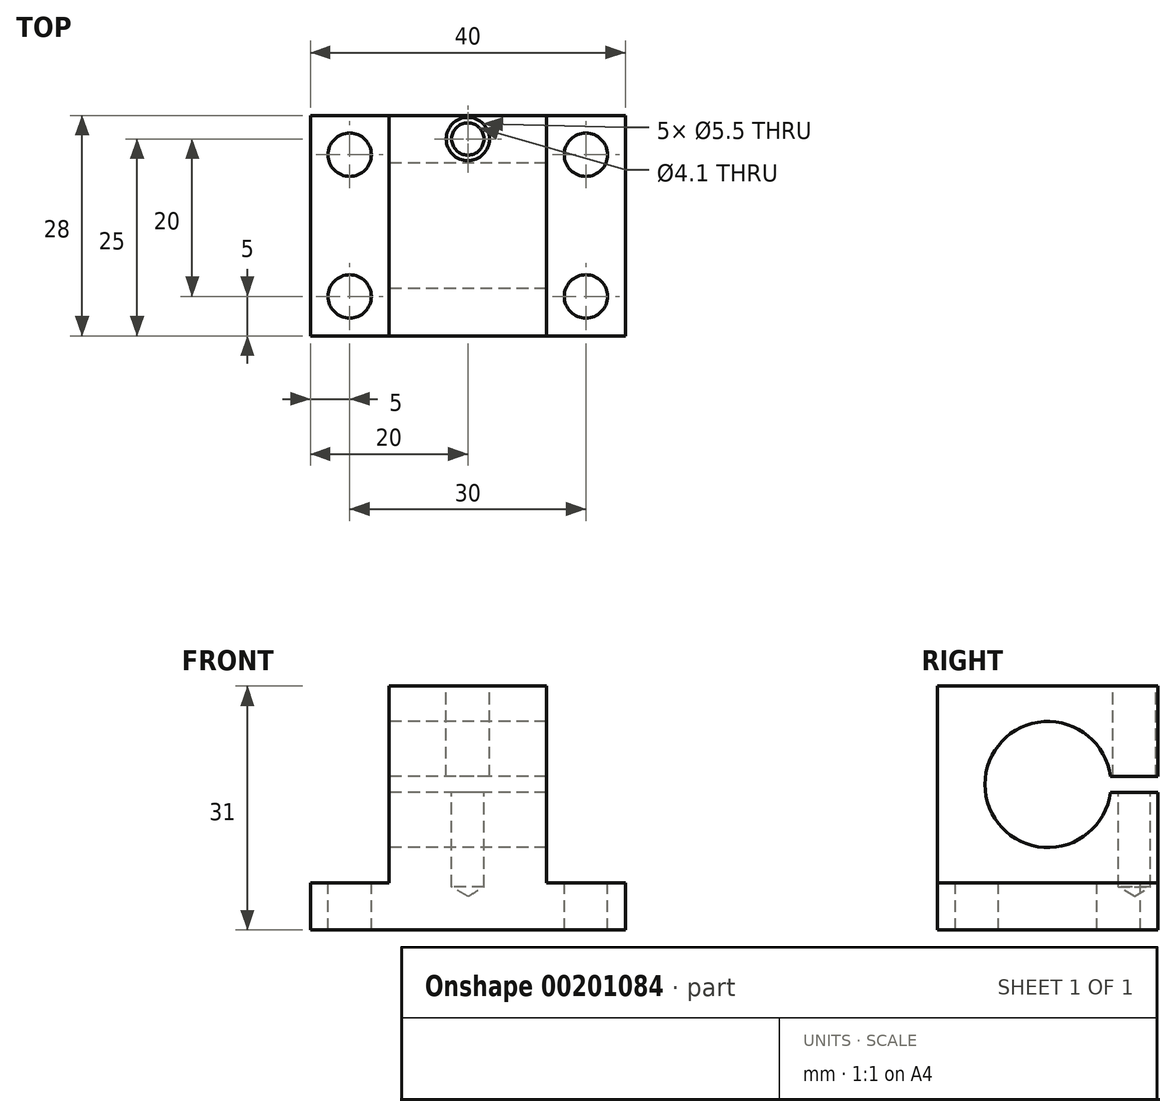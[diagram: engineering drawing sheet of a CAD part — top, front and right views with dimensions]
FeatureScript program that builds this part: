
annotation { "Feature Type Name" : "Feature", "Feature Type Description" : "" }
export const myFeature = defineFeature(function(context is Context, id is Id, definition is map)
    precondition{}
    {
        {
            var Q0;
            Q0=qCreatedBy(makeId("Top.planeOp"),FACE);
            var sketch = newSketch(context, id + "F0", { "sketchPlane" : qUnion([Q0])});
            skLineSegment(sketch, "E0.bottom", {"start": v(0, 0) * mm, "end": v(40, 0) * mm});
            skLineSegment(sketch, "E0.top", {"start": v(0, 28) * mm, "end": v(40, 28) * mm});
            skLineSegment(sketch, "E0.left", {"start": v(0, 0) * mm, "end": v(0, 28) * mm});
            skLineSegment(sketch, "E0.right", {"start": v(40, 0) * mm, "end": v(40, 28) * mm});
            skSolve(sketch);
        }
        {
            var Q0;
            Q0=makeQuery(id+"F0.imprint","IMPRINT",FACE,{"disambiguationData":[TD([[makeQuery(id+"F0.imprint","IMPRINT",EDGE,{"derivedFrom":sQuery(id+"F0.wireOp",EDGE,"E0.bottom")}),1.0]])]});
            extrude(context, id + "F1", {"entities" : qUnion([Q0]), "depth" : 6 * mm});
        }
        {
            var Q0;
            Q0=makeQuery(id+"F1.opExtrude","CAP_FACE",FACE,{"disambiguationData":[OSD([sQuery(id+"F0.wireOp",EDGE,"E0.bottom"),sQuery(id+"F0.wireOp",EDGE,"E0.top"),sQuery(id+"F0.wireOp",EDGE,"E0.left"),sQuery(id+"F0.wireOp",EDGE,"E0.right")])],"isStart":false});
            var sketch = newSketch(context, id + "F2", { "sketchPlane" : qUnion([Q0])});
            skLineSegment(sketch, "E1.bottom", {"start": v(10, 0) * mm, "end": v(30, 0) * mm});
            skLineSegment(sketch, "E1.top", {"start": v(10, 28) * mm, "end": v(30, 28) * mm});
            skLineSegment(sketch, "E1.left", {"start": v(10, 0) * mm, "end": v(10, 28) * mm});
            skLineSegment(sketch, "E1.right", {"start": v(30, 0) * mm, "end": v(30, 28) * mm});
            skSolve(sketch);
        }
        {
            var Q0;
            Q0=makeQuery(id+"F2.imprint","IMPRINT",FACE,{"disambiguationData":[TD([[makeQuery(id+"F2.imprint","IMPRINT",EDGE,{"derivedFrom":sQuery(id+"F2.wireOp",EDGE,"E1.bottom")}),1.0]])]});
            extrude(context, id + "F3", {"entities" : qUnion([Q0]), "operationType" : NewBodyOperationType.ADD, "depth" : 25 * mm});
        }
        {
            var Q0;
            Q0=makeQuery(id+"F3.opExtrude","SWEPT_FACE",FACE,{"disambiguationData":[OSD([sQuery(id+"F2.wireOp",EDGE,"E1.left")])]});
            var sketch = newSketch(context, id + "F4", { "sketchPlane" : qUnion([Q0])});
            skArc(sketch, "E2", {"start": v(-21.94, 17.5) * mm, "mid": v(-6, 18.5) * mm, "end": v(-21.94, 19.5) * mm});
            skPoint(sketch, "E2.centerSnap0", {"position": v(-14, 31) * mm});
            skPoint(sketch, "E2.centerSnap1", {"position": v(-28, 18.5) * mm});
            skLineSegment(sketch, "E3.0", {"start": v(-21.94, 19.5) * mm, "end": v(-32.37, 19.5) * mm});
            skLineSegment(sketch, "E4.0", {"start": v(-21.94, 17.5) * mm, "end": v(-32.37, 17.5) * mm});
            skLineSegment(sketch, "E5", {"start": v(-32.37, 17.5) * mm, "end": v(-32.37, 19.5) * mm});
            skSolve(sketch);
        }
        {
            var Q0;
            {var subQ0=sQuery(id+"F4.wireOp",EDGE,"E2");Q0=makeQuery(id+"F4.imprint","IMPRINT",FACE,{"disambiguationData":[TD([[makeQuery(id+"F4.imprint","IMPRINT",EDGE,{"derivedFrom":subQ0}),1.0]])]});}
            extrude(context, id + "F5", {"entities" : qUnion([Q0]), "operationType" : NewBodyOperationType.REMOVE, "endBound" : BoundingType.THROUGH_ALL, "oppositeDirection" : true, "depth" : 25 * mm});
        }
        {
            var Q0;
            Q0=makeQuery(id+"F5.boolean.opBoolean","COPY",FACE,{"derivedFrom":makeQuery(id+"F5.opExtrude","SWEPT_FACE",FACE,{"disambiguationData":[OSD([sQuery(id+"F4.wireOp",EDGE,"E4.0")])]})});
            var sketch = newSketch(context, id + "F6", { "sketchPlane" : qUnion([Q0])});
            skPoint(sketch, "E6", {"position": v(20, 25) * mm});
            skSolve(sketch);
        }
        {
            var Q0;
            Q0=sQuery(id+"F6.wireOp",VERTEX,"E6");
            var Q1;
            Q1=makeQuery(id+"F1.opExtrude","SWEPT_BODY",BODY,{"disambiguationData":[OSD([sQuery(id+"F0.wireOp",EDGE,"E0.bottom"),sQuery(id+"F0.wireOp",EDGE,"E0.top"),sQuery(id+"F0.wireOp",EDGE,"E0.left"),sQuery(id+"F0.wireOp",EDGE,"E0.right")])]});
            hole(context, id + "F7", {"style" : HoleStyle.SIMPLE, "endStyle" : HoleEndStyle.BLIND, "standardTappedOrClearance" : lookupTablePath({ "standard" : "ISO", "engagement" : "75%", "pitch" : "0.9 mm", "size" : "M5", "type" : "Tapped" }), "standardBlindInLast" : lookupTablePath({ "standard" : "ISO", "engagement" : "75%", "pitch" : "0.9 mm", "size" : "M5", "type" : "Tapped" }), "holeDiameter" : 4.1 * mm, "holeDepth" : 12 * mm, "locations" : qUnion([Q0]), "scope" : qUnion([Q1])});
        }
        {
            var Q0;
            Q0=makeQuery(id+"F3.opExtrude","CAP_FACE",FACE,{"disambiguationData":[OSD([sQuery(id+"F2.wireOp",EDGE,"E1.bottom"),sQuery(id+"F2.wireOp",EDGE,"E1.top"),sQuery(id+"F2.wireOp",EDGE,"E1.left"),sQuery(id+"F2.wireOp",EDGE,"E1.right")])],"isStart":false});
            var sketch = newSketch(context, id + "F8", { "sketchPlane" : qUnion([Q0])});
            skPoint(sketch, "E7", {"position": v(20, 25) * mm});
            skSolve(sketch);
        }
        {
            var Q0;
            Q0=sQuery(id+"F8.wireOp",VERTEX,"E7");
            var Q1;
            Q1=makeQuery(id+"F1.opExtrude","SWEPT_BODY",BODY,{"disambiguationData":[OSD([sQuery(id+"F0.wireOp",EDGE,"E0.bottom"),sQuery(id+"F0.wireOp",EDGE,"E0.top"),sQuery(id+"F0.wireOp",EDGE,"E0.left"),sQuery(id+"F0.wireOp",EDGE,"E0.right")])]});
            hole(context, id + "F9", {"style" : HoleStyle.SIMPLE, "endStyle" : HoleEndStyle.BLIND, "standardTappedOrClearance" : lookupTablePath({ "standard" : "ISO", "size" : "5.5", "type" : "Drilled" }), "standardBlindInLast" : lookupTablePath({ "standard" : "ISO", "size" : "5.5", "type" : "Drilled" }), "holeDiameter" : 5.5 * mm, "holeDepth" : 12 * mm, "locations" : qUnion([Q0]), "scope" : qUnion([Q1])});
        }
        {
            var Q0;
            {var subQ0=sQuery(id+"F0.wireOp",EDGE,"E0.left");var subQ1=sQuery(id+"F0.wireOp",EDGE,"E0.top");var subQ2=sQuery(id+"F0.wireOp",EDGE,"E0.bottom");Q0=makeQuery(id+"F3.boolean.opBoolean","SPLIT",FACE,{"disambiguationData":[TD([makeQuery(id+"F1.opExtrude","SWEPT_FACE",FACE,{"disambiguationData":[OSD([subQ0])]})])],"derivedFrom":makeQuery(id+"F1.opExtrude","CAP_FACE",FACE,{"disambiguationData":[OSD([subQ2,subQ1,subQ0,sQuery(id+"F0.wireOp",EDGE,"E0.right")])],"isStart":false})});}
            var sketch = newSketch(context, id + "F10", { "sketchPlane" : qUnion([Q0])});
            skCircle(sketch, "E8", {"center": v(5, 5) * mm, "radius": 1.5 * mm, "construction": true});
            skCircle(sketch, "E9", {"center": v(5, 23) * mm, "radius": 1.5 * mm, "construction": true});
            skCircle(sketch, "E10", {"center": v(35, 5) * mm, "radius": 1.5 * mm, "construction": true});
            skCircle(sketch, "E11", {"center": v(35, 23) * mm, "radius": 1.5 * mm, "construction": true});
            skLineSegment(sketch, "E12", {"start": v(5, 0) * mm, "end": v(5, 28) * mm, "construction": true});
            skLineSegment(sketch, "E13", {"start": v(35, 27.98) * mm, "end": v(35, 0) * mm, "construction": true});
            skSolve(sketch);
        }
        {
            var Q0;
            Q0=sQuery(id+"F10.wireOp",VERTEX,"E8.center");
            var Q1;
            Q1=sQuery(id+"F10.wireOp",VERTEX,"E9.center");
            var Q2;
            Q2=sQuery(id+"F10.wireOp",VERTEX,"E11.center");
            var Q3;
            Q3=sQuery(id+"F10.wireOp",VERTEX,"E10.center");
            var Q4;
            Q4=makeQuery(id+"F1.opExtrude","SWEPT_BODY",BODY,{"disambiguationData":[OSD([sQuery(id+"F0.wireOp",EDGE,"E0.bottom"),sQuery(id+"F0.wireOp",EDGE,"E0.top"),sQuery(id+"F0.wireOp",EDGE,"E0.left"),sQuery(id+"F0.wireOp",EDGE,"E0.right")])]});
            hole(context, id + "F11", {"style" : HoleStyle.SIMPLE, "endStyle" : HoleEndStyle.BLIND, "standardTappedOrClearance" : lookupTablePath({ "standard" : "ISO", "size" : "5.5", "type" : "Drilled" }), "standardBlindInLast" : lookupTablePath({ "standard" : "ISO", "size" : "5.5", "type" : "Drilled" }), "holeDiameter" : 5.5 * mm, "holeDepth" : 12 * mm, "locations" : qUnion([Q0, Q1, Q2, Q3]), "scope" : qUnion([Q4])});
        }
    });
